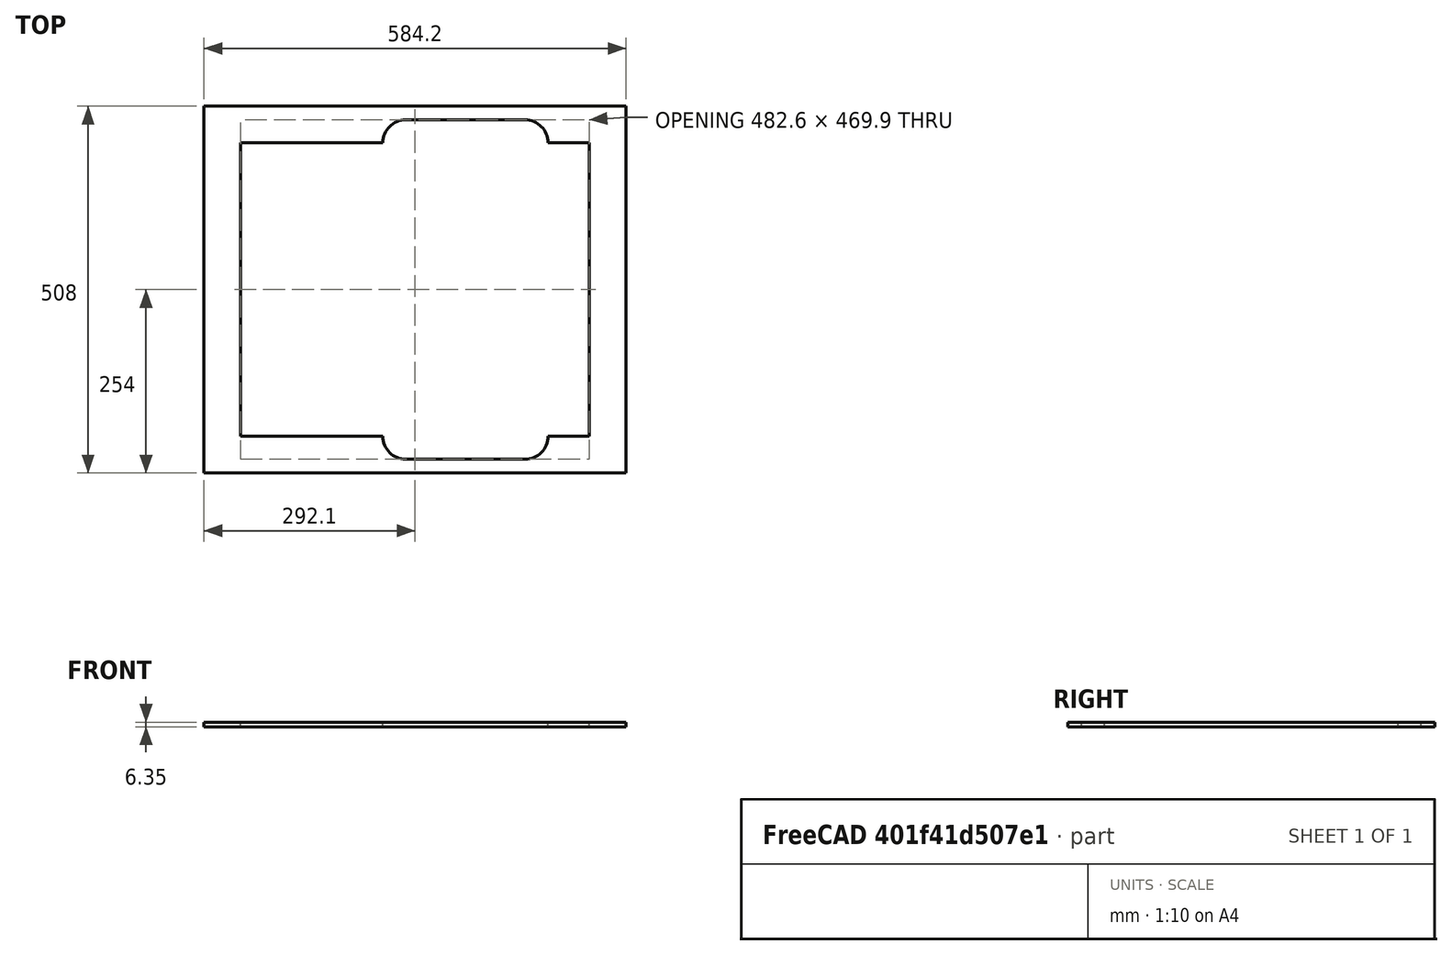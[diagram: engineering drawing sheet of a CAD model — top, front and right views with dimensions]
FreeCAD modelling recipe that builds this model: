
FCSTD DOCUMENT  (FreeCAD 0.16R6712 (Git))
Label: sides
License: All rights reserved
LicenseURL: http://en.wikipedia.org/wiki/All_rights_reserved
objects: Sketcher::SketchObject×1, PartDesign::Pad×1
note: 3 computed .brp shape members not serialized (recipe doc carries the construction recipe); baked Part::Feature solids carry a one-line shape summary decoded from their .brp

FEATURE [Sketcher::SketchObject] Sketch  label="sides pattern"
  Placement = pos=(914.4,1066.8,914.4) rot=(0,0,1;0rad)
  sketch-geometry (30):
    g0: LineSegment StartX=-292.1 StartY=254 StartZ=0 EndX=292.1 EndY=254 EndZ=0
    g1: LineSegment StartX=292.1 StartY=254 StartZ=0 EndX=292.1 EndY=-254 EndZ=0
    g2: LineSegment StartX=292.1 StartY=-254 StartZ=0 EndX=-292.1 EndY=-254 EndZ=0
    g3: LineSegment StartX=-292.1 StartY=-254 StartZ=0 EndX=-292.1 EndY=254 EndZ=0
    g4: LineSegment StartX=241.3 StartY=-203.2 StartZ=0 EndX=241.3 EndY=203.2 EndZ=0
    g5: LineSegment StartX=-241.3 StartY=203.2 StartZ=0 EndX=-241.3 EndY=-203.2 EndZ=0
    g6: LineSegment StartX=-241.3 StartY=203.2 StartZ=0 EndX=-44.45 EndY=203.2 EndZ=0
    g7: LineSegment StartX=241.3 StartY=203.2 StartZ=0 EndX=184.15 EndY=203.2 EndZ=0
    g8: ArcOfCircle CenterX=152.4 CenterY=203.2 CenterZ=0 NormalX=0 NormalY=0 NormalZ=1 Radius=31.75 StartAngle=0 EndAngle=1.5708
    g9: LineSegment [constr] StartX=184.15 StartY=203.2 StartZ=0 EndX=152.4 EndY=203.2 EndZ=0
    g10: ArcOfCircle CenterX=-12.7 CenterY=203.2 CenterZ=0 NormalX=0 NormalY=0 NormalZ=1 Radius=31.75 StartAngle=1.5708 EndAngle=3.14159
    g11: LineSegment [constr] StartX=-44.45 StartY=203.2 StartZ=0 EndX=-12.7 EndY=203.2 EndZ=0
    g12: LineSegment [constr] StartX=-12.7 StartY=203.2 StartZ=0 EndX=152.4 EndY=203.2 EndZ=0
    g13: LineSegment StartX=-12.7 StartY=234.95 StartZ=0 EndX=152.4 EndY=234.95 EndZ=0
    g14: LineSegment [constr] StartX=-12.7 StartY=203.2 StartZ=0 EndX=-12.7 EndY=234.95 EndZ=0
    g15: LineSegment [constr] StartX=152.4 StartY=203.2 StartZ=0 EndX=152.4 EndY=234.95 EndZ=0
    g16: LineSegment StartX=-241.3 StartY=-203.2 StartZ=0 EndX=-44.45 EndY=-203.2 EndZ=0
    g17: LineSegment [constr] StartX=-44.45 StartY=-203.2 StartZ=0 EndX=-12.7 EndY=-203.2 EndZ=0
    g18: LineSegment [constr] StartX=-12.7 StartY=-203.2 StartZ=0 EndX=152.4 EndY=-203.2 EndZ=0
    g19: LineSegment [constr] StartX=152.4 StartY=-203.2 StartZ=0 EndX=184.15 EndY=-203.2 EndZ=0
    g20: LineSegment StartX=241.3 StartY=-203.2 StartZ=0 EndX=184.15 EndY=-203.2 EndZ=0
    g21: LineSegment [constr] StartX=-12.7 StartY=-203.2 StartZ=0 EndX=-12.7 EndY=-234.95 EndZ=0
    g22: LineSegment [constr] StartX=152.4 StartY=-203.2 StartZ=0 EndX=152.4 EndY=-234.95 EndZ=0
    g23: ArcOfCircle CenterX=-12.7 CenterY=-203.2 CenterZ=0 NormalX=0 NormalY=0 NormalZ=1 Radius=31.75 StartAngle=3.14159 EndAngle=4.71239
    g24: ArcOfCircle CenterX=152.4 CenterY=-203.2 CenterZ=0 NormalX=0 NormalY=0 NormalZ=1 Radius=31.75 StartAngle=4.71239 EndAngle=6.28319
    g25: LineSegment StartX=-12.7 StartY=-234.95 StartZ=0 EndX=152.4 EndY=-234.95 EndZ=0
    g26: LineSegment [constr] StartX=241.3 StartY=-203.2 StartZ=0 EndX=292.1 EndY=-203.2 EndZ=0
    g27: LineSegment [constr] StartX=241.3 StartY=-203.2 StartZ=0 EndX=241.3 EndY=-254 EndZ=0
    g28: LineSegment [constr] StartX=-241.3 StartY=203.2 StartZ=0 EndX=-241.3 EndY=254 EndZ=0
    g29: LineSegment [constr] StartX=-241.3 StartY=203.2 StartZ=0 EndX=-292.1 EndY=203.2 EndZ=0
  constraints (89):
    c: Coincident(g0,g1)
    c: Coincident(g1,g2)
    c: Coincident(g2,g3)
    c: Coincident(g3,g0)
    c: Horizontal(g2)
    c: Vertical(g1)
    c: Equal(g3,g1)
    c: Equal(g0,g2)
    c: Symmetric(g0,g1,g-1)
    c: Vertical(g5)
    c: Equal(g5,g4)
    c: DistanceY(g3,g3) = 508
    c: DistanceX(g2,g2) = 584.2
    c: DistanceY(g5,g5) = 406.4
    c: Symmetric(g4,g4,g-1)
    c: Coincident(g6,g5)
    c: Horizontal(g6)
    c: Coincident(g7,g4)
    c: Horizontal(g7)
    c: Coincident(g8,g7)
    c: Coincident(g9,g7)
    c: Coincident(g9,g8)
    c: Horizontal(g9)
    c: Coincident(g10,g6)
    c: Coincident(g11,g6)
    c: Coincident(g11,g10)
    c: Equal(g11,g9)
    c: Coincident(g12,g10)
    c: Coincident(g12,g8)
    c: Coincident(g13,g10)
    c: Coincident(g13,g8)
    c: DistanceX(g13,g13) = 165.1
    c: Coincident(g14,g10)
    c: Coincident(g14,g10)
    c: Vertical(g14)
    c: Coincident(g15,g8)
    c: Coincident(g15,g8)
    c: Vertical(g15)
    c: Equal(g14,g15)
    c: DistanceY(g14,g14) = 31.75
    c: Horizontal(g12)
    c: DistanceX(g8,g0) = 139.7
    c: Coincident(g16,g5)
    c: Horizontal(g16)
    c: Equal(g16,g6)
    c: Coincident(g17,g16)
    c: Horizontal(g17)
    c: Coincident(g18,g17)
    c: Horizontal(g19)
    c: Coincident(g20,g4)
    c: Coincident(g20,g19)
    c: Horizontal(g20)
    c: Equal(g7,g20)
    c: Coincident(g19,g18)
    c: Equal(g18,g12)
    c: Equal(g19,g17)
    c: Equal(g17,g11)
    c: Coincident(g21,g17)
    c: Vertical(g21)
    c: Coincident(g22,g18)
    c: Vertical(g22)
    c: Equal(g22,g21)
    c: Equal(g21,g15)
    c: Coincident(g23,g17)
    c: Coincident(g23,g16)
    c: Coincident(g23,g21)
    c: Coincident(g24,g18)
    c: Coincident(g24,g19)
    c: Coincident(g24,g22)
    c: Coincident(g25,g21)
    c: Coincident(g25,g22)
    c: Horizontal(g25)
    c: Equal(g25,g13)
    c: Coincident(g26,g4)
    c: PointOnObject(g26,g1)
    c: Horizontal(g26)
    c: Coincident(g27,g4)
    c: PointOnObject(g27,g2)
    c: Vertical(g27)
    c: PointOnObject(g28,g0)
    c: Vertical(g28)
    c: Symmetric(g5,g4,g-1)
    c: Coincident(g28,g5)
    c: Coincident(g29,g5)
    c: PointOnObject(g29,g3)
    c: Horizontal(g29)
    c: Equal(g29,g28)
    c: Equal(g28,g26)
    c: Equal(g26,g27)
FEATURE [PartDesign::Pad] Pad  label="sides"
  Length = 6.35
  Length2 = 100
  Placement = pos=(914.4,1066.8,914.4) rot=(0,0,1;0rad)
  Sketch = -> Sketch
  Type = 0
